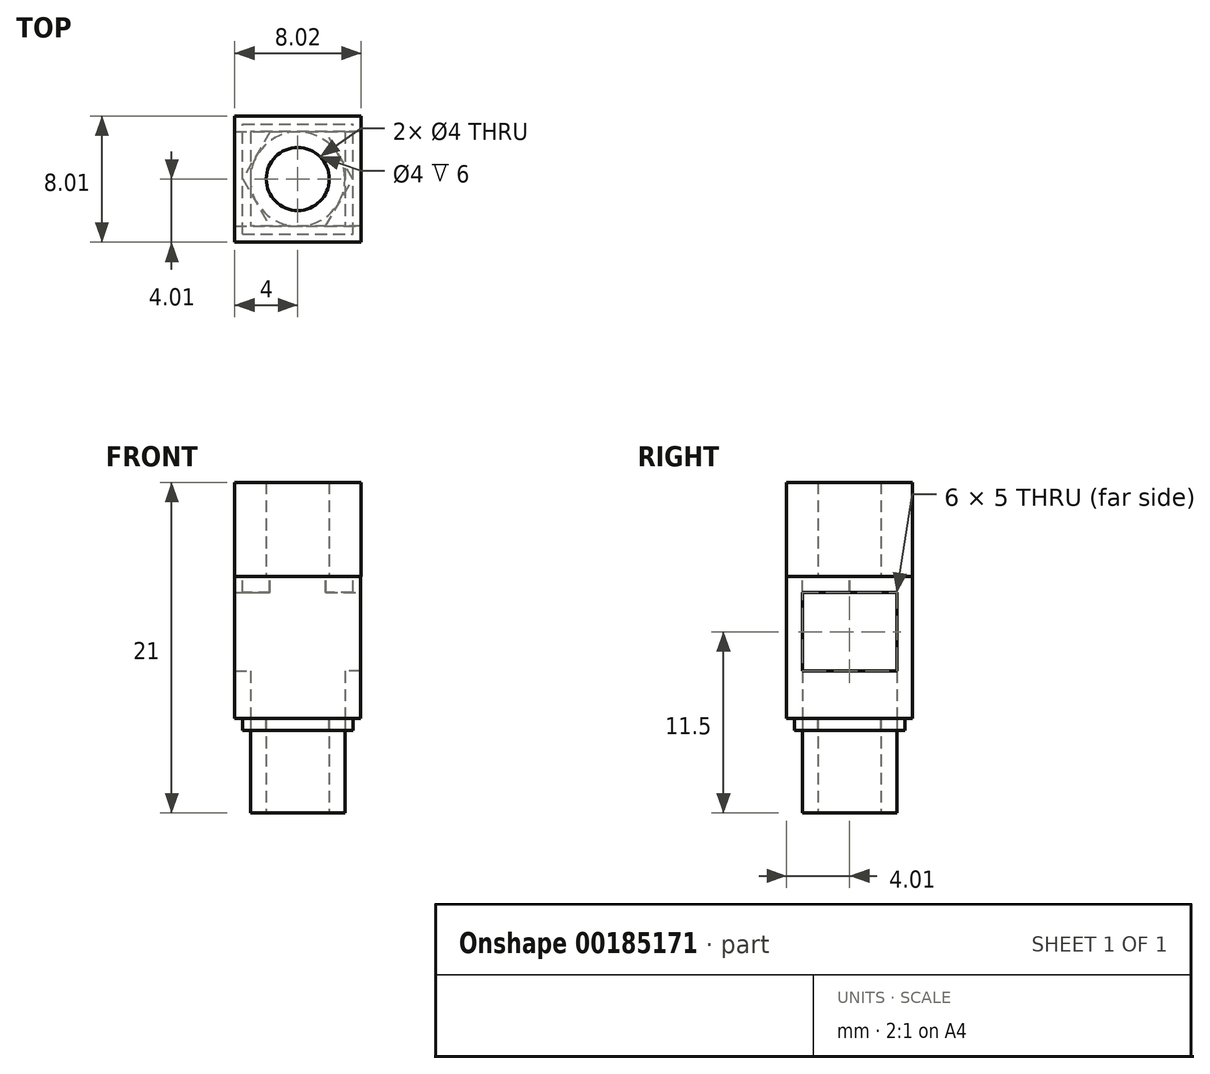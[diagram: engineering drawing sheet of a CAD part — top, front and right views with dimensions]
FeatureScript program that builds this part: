
annotation { "Feature Type Name" : "Feature", "Feature Type Description" : "" }
export const myFeature = defineFeature(function(context is Context, id is Id, definition is map)
    precondition{}
    {
        {
            var Q0;
            Q0=qCreatedBy(makeId("Top.planeOp"),FACE);
            var sketch = newSketch(context, id + "F0", { "sketchPlane" : qUnion([Q0])});
            skCircle(sketch, "E0", {"center": v(0, 0) * mm, "radius": 2 * mm});
            skCircle(sketch, "E1", {"center": v(0, 0) * mm, "radius": 3 * mm});
            skSolve(sketch);
        }
        {
            var Q0;
            Q0 = qSketchRegion(id + "F0", true);
            extrude(context, id + "F1", {"entities" : qUnion([Q0]), "depth" : 6 * mm});
        }
        {
            var Q0;
            Q0=makeQuery(id+"F1.opExtrude","CAP_FACE",FACE,{"disambiguationData":[OSD([sQuery(id+"F0.wireOp",EDGE,"E0"),sQuery(id+"F0.wireOp",EDGE,"E1")])],"isStart":false});
            var sketch = newSketch(context, id + "F2", { "sketchPlane" : qUnion([Q0])});
            skLineSegment(sketch, "E2.bottom", {"start": v(4, 4) * mm, "end": v(-4, 4) * mm});
            skLineSegment(sketch, "E2.top", {"start": v(4, -4) * mm, "end": v(-4, -4) * mm});
            skLineSegment(sketch, "E2.left", {"start": v(4, 4) * mm, "end": v(4, -4) * mm});
            skLineSegment(sketch, "E2.right", {"start": v(-4, 4) * mm, "end": v(-4, -4) * mm});
            skPoint(sketch, "E2.middle", {"position": v(0, 0) * mm});
            skLineSegment(sketch, "E3.bottom", {"start": v(3, 3) * mm, "end": v(-3, 3) * mm});
            skLineSegment(sketch, "E3.top", {"start": v(3, -3) * mm, "end": v(-3, -3) * mm});
            skLineSegment(sketch, "E3.left", {"start": v(3, 3) * mm, "end": v(3, -3) * mm});
            skLineSegment(sketch, "E3.right", {"start": v(-3, 3) * mm, "end": v(-3, -3) * mm});
            skSolve(sketch);
        }
        {
            var Q0;
            Q0=makeQuery(id+"F2.imprint","IMPRINT",FACE,{"disambiguationData":[TD([[makeQuery(id+"F2.imprint","IMPRINT",EDGE,{"derivedFrom":sQuery(id+"F2.wireOp",EDGE,"E2.bottom")}),1.0]])]});
            extrude(context, id + "F3", {"entities" : qUnion([Q0]), "depth" : 3 * mm});
        }
        {
            var Q0;
            Q0=makeQuery(id+"F3.opExtrude","CAP_FACE",FACE,{"disambiguationData":[OSD([sQuery(id+"F2.wireOp",EDGE,"E2.bottom"),sQuery(id+"F2.wireOp",EDGE,"E2.top"),sQuery(id+"F2.wireOp",EDGE,"E2.left"),sQuery(id+"F2.wireOp",EDGE,"E2.right"),sQuery(id+"F2.wireOp",EDGE,"E3.bottom"),sQuery(id+"F2.wireOp",EDGE,"E3.top"),sQuery(id+"F2.wireOp",EDGE,"E3.left"),sQuery(id+"F2.wireOp",EDGE,"E3.right")])],"isStart":true});
            var sketch = newSketch(context, id + "F4", { "sketchPlane" : qUnion([Q0])});
            skLineSegment(sketch, "E4", {"start": v(-4, 4) * mm, "end": v(-3, 3) * mm});
            skLineSegment(sketch, "E5", {"start": v(4, -4) * mm, "end": v(3, -3) * mm});
            skLineSegment(sketch, "E6.bottom", {"start": v(-3.5, 3.5) * mm, "end": v(3.5, 3.5) * mm});
            skLineSegment(sketch, "E6.top", {"start": v(-3.5, -3.5) * mm, "end": v(3.5, -3.5) * mm});
            skLineSegment(sketch, "E6.left", {"start": v(-3.5, 3.5) * mm, "end": v(-3.5, -3.5) * mm});
            skLineSegment(sketch, "E6.right", {"start": v(3.5, 3.5) * mm, "end": v(3.5, -3.5) * mm});
            skCircle(sketch, "E7", {"center": v(0, 0) * mm, "radius": 2 * mm});
            skSolve(sketch);
        }
        {
            var Q0;
            {var subQ1=sQuery(id+"F4.wireOp",EDGE,"E6.bottom");Q0=makeQuery(id+"F4.imprint","IMPRINT",FACE,{"disambiguationData":[TD([[makeQuery(id+"F4.imprint","IMPRINT",EDGE,{"derivedFrom":subQ1}),-1.0]])]});}
            var Q1;
            Q1=makeQuery(id+"F4.imprint","IMPRINT",FACE,{"disambiguationData":[TD([[makeQuery(id+"F4.imprint","IMPRINT",EDGE,{"derivedFrom":sQuery(id+"F4.wireOp",EDGE,"E7")}),-1.0]])]});
            var Q2;
            {var subQ2=sQuery(id+"F4.wireOp",EDGE,"E6.top");Q2=makeQuery(id+"F4.imprint","IMPRINT",FACE,{"disambiguationData":[TD([[makeQuery(id+"F4.imprint","IMPRINT",EDGE,{"derivedFrom":subQ2}),1.0]])]});}
            extrude(context, id + "F5", {"entities" : qUnion([Q0, Q1, Q2]), "depth" : .75 * mm});
        }
        {
            var Q0;
            Q0=makeQuery(id+"F3.opExtrude","CAP_FACE",FACE,{"disambiguationData":[OSD([sQuery(id+"F2.wireOp",EDGE,"E2.bottom"),sQuery(id+"F2.wireOp",EDGE,"E2.top"),sQuery(id+"F2.wireOp",EDGE,"E2.left"),sQuery(id+"F2.wireOp",EDGE,"E2.right"),sQuery(id+"F2.wireOp",EDGE,"E3.bottom"),sQuery(id+"F2.wireOp",EDGE,"E3.top"),sQuery(id+"F2.wireOp",EDGE,"E3.left"),sQuery(id+"F2.wireOp",EDGE,"E3.right")])],"isStart":false});
            var sketch = newSketch(context, id + "F6", { "sketchPlane" : qUnion([Q0])});
            skLineSegment(sketch, "E8.bottom", {"start": v(-4, 4) * mm, "end": v(-3, 4) * mm});
            skLineSegment(sketch, "E8.top", {"start": v(-4, 3) * mm, "end": v(-3, 3) * mm});
            skLineSegment(sketch, "E8.left", {"start": v(-4, 4) * mm, "end": v(-4, 3) * mm});
            skLineSegment(sketch, "E8.right", {"start": v(-3, 4) * mm, "end": v(-3, 3) * mm});
            skLineSegment(sketch, "E9.bottom", {"start": v(-4, -4) * mm, "end": v(-3, -4) * mm});
            skLineSegment(sketch, "E9.top", {"start": v(-4, -3) * mm, "end": v(-3, -3) * mm});
            skLineSegment(sketch, "E9.left", {"start": v(-4, -4) * mm, "end": v(-4, -3) * mm});
            skLineSegment(sketch, "E9.right", {"start": v(-3, -4) * mm, "end": v(-3, -3) * mm});
            skLineSegment(sketch, "E10.bottom", {"start": v(4, -4) * mm, "end": v(3, -4) * mm});
            skLineSegment(sketch, "E10.top", {"start": v(4, -3) * mm, "end": v(3, -3) * mm});
            skLineSegment(sketch, "E10.left", {"start": v(4, -4) * mm, "end": v(4, -3) * mm});
            skLineSegment(sketch, "E10.right", {"start": v(3, -4) * mm, "end": v(3, -3) * mm});
            skLineSegment(sketch, "E11.bottom", {"start": v(4, 4) * mm, "end": v(3, 4) * mm});
            skLineSegment(sketch, "E11.top", {"start": v(4, 3) * mm, "end": v(3, 3) * mm});
            skLineSegment(sketch, "E11.left", {"start": v(4, 4) * mm, "end": v(4, 3) * mm});
            skLineSegment(sketch, "E11.right", {"start": v(3, 4) * mm, "end": v(3, 3) * mm});
            skSolve(sketch);
        }
        {
            var Q0;
            Q0=makeQuery(id+"F6.imprint","IMPRINT",FACE,{"disambiguationData":[TD([[makeQuery(id+"F6.imprint","IMPRINT",EDGE,{"derivedFrom":sQuery(id+"F6.wireOp",EDGE,"E8.bottom")}),1.0]])]});
            var Q1;
            Q1=makeQuery(id+"F6.imprint","IMPRINT",FACE,{"disambiguationData":[TD([[makeQuery(id+"F6.imprint","IMPRINT",EDGE,{"derivedFrom":sQuery(id+"F6.wireOp",EDGE,"E11.bottom")}),1.0]])]});
            var Q2;
            Q2=makeQuery(id+"F6.imprint","IMPRINT",FACE,{"disambiguationData":[TD([[makeQuery(id+"F6.imprint","IMPRINT",EDGE,{"derivedFrom":sQuery(id+"F6.wireOp",EDGE,"E10.bottom")}),-1.0]])]});
            var Q3;
            Q3=makeQuery(id+"F6.imprint","IMPRINT",FACE,{"disambiguationData":[TD([[makeQuery(id+"F6.imprint","IMPRINT",EDGE,{"derivedFrom":sQuery(id+"F6.wireOp",EDGE,"E9.bottom")}),-1.0]])]});
            extrude(context, id + "F7", {"entities" : qUnion([Q0, Q1, Q2, Q3]), "operationType" : NewBodyOperationType.ADD, "depth" : 6 * mm});
        }
        {
            var Q0;
            Q0=makeQuery(id+"F7.opExtrude","CAP_FACE",FACE,{"disambiguationData":[OSD([sQuery(id+"F6.wireOp",EDGE,"E8.bottom"),sQuery(id+"F6.wireOp",EDGE,"E8.top"),sQuery(id+"F6.wireOp",EDGE,"E8.left"),sQuery(id+"F6.wireOp",EDGE,"E8.right")])],"isStart":false});
            var sketch = newSketch(context, id + "F8", { "sketchPlane" : qUnion([Q0])});
            skLineSegment(sketch, "E12.bottom", {"start": v(-4, 4) * mm, "end": v(4.02, 4) * mm});
            skLineSegment(sketch, "E12.top", {"start": v(-4, -4.01) * mm, "end": v(4.02, -4.01) * mm});
            skLineSegment(sketch, "E12.left", {"start": v(-4, 4) * mm, "end": v(-4, -4.01) * mm});
            skLineSegment(sketch, "E12.right", {"start": v(4.02, 4) * mm, "end": v(4.02, -4.01) * mm});
            skCircle(sketch, "E13", {"center": v(0, 0) * mm, "radius": 2 * mm});
            skSolve(sketch);
        }
        {
            var Q0;
            {var subQ4=makeQuery(id+"F7.opExtrude","CAP_EDGE",EDGE,{"disambiguationData":[OSD([sQuery(id+"F6.wireOp",EDGE,"E8.top")])],"isStart":false});Q0=makeQuery(id+"F8.imprint","IMPRINT",FACE,{"disambiguationData":[TD([[makeQuery(id+"F8.imprint","IMPRINT",EDGE,{"derivedFrom":subQ4}),1.0]])]});}
            var Q1;
            {var subQ4=sQuery(id+"F8.wireOp",EDGE,"E12.top");Q1=makeQuery(id+"F8.imprint","IMPRINT",FACE,{"disambiguationData":[TD([[makeQuery(id+"F8.imprint","IMPRINT",EDGE,{"derivedFrom":subQ4}),1.0]])]});}
            extrude(context, id + "F9", {"entities" : qUnion([Q0, Q1]), "operationType" : NewBodyOperationType.ADD, "depth" : 6 * mm});
        }
        {
            var Q0;
            Q0=makeQuery(id+"F9.opExtrude","CAP_FACE",FACE,{"disambiguationData":[OSD([sQuery(id+"F8.wireOp",EDGE,"E12.bottom"),sQuery(id+"F8.wireOp",EDGE,"E12.top"),sQuery(id+"F8.wireOp",EDGE,"E12.left"),sQuery(id+"F8.wireOp",EDGE,"E12.right"),sQuery(id+"F8.wireOp",EDGE,"E13")])],"isStart":true});
            var sketch = newSketch(context, id + "F10", { "sketchPlane" : qUnion([Q0])});
            skLineSegment(sketch, "E14.bottom", {"start": v(-3, 3) * mm, "end": v(3, 3) * mm});
            skLineSegment(sketch, "E14.top", {"start": v(-3, 4) * mm, "end": v(3, 4) * mm});
            skLineSegment(sketch, "E14.left", {"start": v(-3, 3) * mm, "end": v(-3, 4) * mm});
            skLineSegment(sketch, "E14.right", {"start": v(3, 3) * mm, "end": v(3, 4) * mm});
            skLineSegment(sketch, "E15.bottom", {"start": v(-3, -4) * mm, "end": v(3, -4) * mm});
            skLineSegment(sketch, "E15.top", {"start": v(-3, -3) * mm, "end": v(3, -3) * mm});
            skLineSegment(sketch, "E15.left", {"start": v(-3, -4) * mm, "end": v(-3, -3) * mm});
            skLineSegment(sketch, "E15.right", {"start": v(3, -4) * mm, "end": v(3, -3) * mm});
            skSolve(sketch);
        }
        {
            var Q0;
            Q0=makeQuery(id+"F10.imprint","IMPRINT",FACE,{"disambiguationData":[TD([[makeQuery(id+"F10.imprint","IMPRINT",EDGE,{"derivedFrom":sQuery(id+"F10.wireOp",EDGE,"E14.bottom")}),1.0]])]});
            var Q1;
            Q1=makeQuery(id+"F10.imprint","IMPRINT",FACE,{"disambiguationData":[TD([[makeQuery(id+"F10.imprint","IMPRINT",EDGE,{"derivedFrom":sQuery(id+"F10.wireOp",EDGE,"E15.bottom")}),-1.0]])]});
            extrude(context, id + "F11", {"entities" : qUnion([Q0, Q1]), "operationType" : NewBodyOperationType.ADD, "depth" : 7.62 * mm});
        }
        {
            var Q0;
            Q0=makeQuery(id+"F9.opExtrude","CAP_FACE",FACE,{"disambiguationData":[OSD([sQuery(id+"F8.wireOp",EDGE,"E12.bottom"),sQuery(id+"F8.wireOp",EDGE,"E12.top"),sQuery(id+"F8.wireOp",EDGE,"E12.left"),sQuery(id+"F8.wireOp",EDGE,"E12.right"),sQuery(id+"F8.wireOp",EDGE,"E13")])],"isStart":true});
            var sketch = newSketch(context, id + "F12", { "sketchPlane" : qUnion([Q0])});
            skCircle(sketch, "E16.cCircle", {"center": v(0, 0) * mm, "radius": 3.03 * mm, "construction": true});
            skLineSegment(sketch, "E16.0", {"start": v(-3.5, -0.03) * mm, "end": v(-1.77, 3.02) * mm});
            skLineSegment(sketch, "E16.1", {"start": v(-1.77, 3.02) * mm, "end": v(1.73, 3.04) * mm});
            skLineSegment(sketch, "E16.2", {"start": v(1.73, 3.04) * mm, "end": v(3.5, 0.03) * mm});
            skLineSegment(sketch, "E16.3", {"start": v(3.5, 0.03) * mm, "end": v(1.77, -3.02) * mm});
            skLineSegment(sketch, "E16.4", {"start": v(1.77, -3.02) * mm, "end": v(-1.73, -3.04) * mm});
            skLineSegment(sketch, "E16.5", {"start": v(-1.73, -3.04) * mm, "end": v(-3.5, -0.03) * mm});
            skPoint(sketch, "E16.0.midPoint", {"position": v(-2.64, 1.5) * mm});
            skLineSegment(sketch, "E17.bottom", {"start": v(4, 3) * mm, "end": v(-4, 3) * mm});
            skLineSegment(sketch, "E17.top", {"start": v(4, -3) * mm, "end": v(-4, -3) * mm});
            skLineSegment(sketch, "E17.left", {"start": v(4, 3) * mm, "end": v(4, -3) * mm});
            skLineSegment(sketch, "E17.right", {"start": v(-4, 3) * mm, "end": v(-4, -3) * mm});
            skSolve(sketch);
        }
        {
            var Q0;
            Q0=makeQuery(id+"F12.imprint","IMPRINT",FACE,{"disambiguationData":[TD([[makeQuery(id+"F12.imprint","IMPRINT",EDGE,{"derivedFrom":sQuery(id+"F12.wireOp",EDGE,"E16.0")}),1.0]])]});
            var Q1;
            {var subQ0=sQuery(id+"F12.wireOp",EDGE,"E17.left");Q1=makeQuery(id+"F12.imprint","IMPRINT",FACE,{"disambiguationData":[TD([[makeQuery(id+"F12.imprint","IMPRINT",EDGE,{"derivedFrom":subQ0}),-1.0]])]});}
            extrude(context, id + "F13", {"entities" : qUnion([Q0, Q1]), "operationType" : NewBodyOperationType.ADD, "depth" : 1 * mm});
        }
    });
